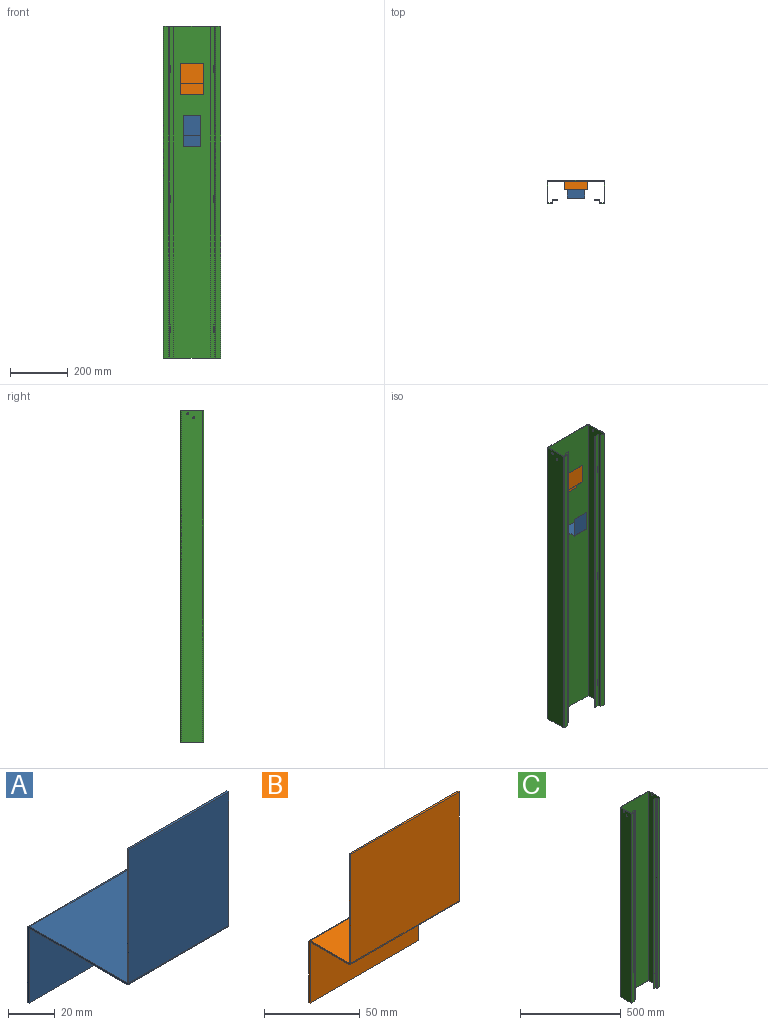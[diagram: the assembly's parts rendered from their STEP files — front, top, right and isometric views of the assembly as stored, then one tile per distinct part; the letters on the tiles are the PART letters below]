
ASSEMBLY  parts=3 mates=2
PART A: 22 faces, bbox 60x61x110 mm
  f0: plane 38.65x1mm, normal (-1,0,0), area 38.7mm2, adj f2,f3,f4,f19
  f1: plane 38.65x1mm, normal (1,0,0), area 38.7mm2, adj f2,f3,f4,f18
  f2: plane 60x1mm, normal (0,0,-1), area 60mm2, adj f0,f1,f3,f4
  f3: plane 60x38.65mm, normal (0,1,0), area 2319mm2, adj f0,f1,f2,f20
  f4: plane 60x38.65mm, normal (0,-1,0), area 2319mm2, adj f0,f1,f2,f21
  f5: plane 58.3x1mm, normal (-1,0,0), area 58.3mm2, adj f7,f8,f15,f19
  f6: plane 58.3x1mm, normal (1,0,0), area 58.3mm2, adj f7,f8,f14,f18
  f7: plane 60x58.3mm, normal (0,0,1), area 3498mm2, adj f5,f6,f17,f20
  f8: plane 60x58.3mm, normal (0,0,-1), area 3498mm2, adj f5,f6,f16,f21
  f9: plane 69.65x1mm, normal (-1,0,0), area 69.7mm2, adj f10,f12,f13,f15
  f10: plane 60x1mm, normal (0,0,1), area 60mm2, adj f9,f11,f12,f13
  f11: plane 69.65x1mm, normal (1,0,0), area 69.7mm2, adj f10,f12,f13,f14
  f12: plane 69.65x60mm, normal (0,1,0), area 4179mm2, adj f9,f10,f11,f17
  f13: plane 69.65x60mm, normal (0,-1,0), area 4179mm2, adj f9,f10,f11,f16
  f14: plane 1.35x1.35mm, normal (1,0,0), area 1.3mm2, adj f6,f11,f16,f17
  f15: plane 1.35x1.35mm, normal (-1,0,0), area 1.3mm2, adj f5,f9,f16,f17
  f16: cylinder r=1.35mm len=60mm, axis (1,0,0), area 127.2mm2, adj f8,f13,f14,f15
  f17: cylinder r=0.35mm len=60mm, axis (1,0,0), area 33mm2, adj f7,f12,f14,f15
  f18: plane 1.35x1.35mm, normal (1,0,0), area 1.3mm2, adj f1,f6,f20,f21
  f19: plane 1.35x1.35mm, normal (-1,0,0), area 1.3mm2, adj f0,f5,f20,f21
  f20: cylinder r=1.35mm len=60mm, axis (1,0,0), area 127.2mm2, adj f3,f7,f18,f19
  f21: cylinder r=0.35mm len=60mm, axis (1,0,0), area 33mm2, adj f4,f8,f18,f19
PART B: 22 faces, bbox 80x31x110 mm
  f0: plane 38.65x1mm, normal (-1,0,0), area 38.7mm2, adj f2,f3,f4,f19
  f1: plane 38.65x1mm, normal (1,0,0), area 38.7mm2, adj f2,f3,f4,f18
  f2: plane 80x1mm, normal (0,0,-1), area 80mm2, adj f0,f1,f3,f4
  f3: plane 80x38.65mm, normal (0,1,0), area 3092mm2, adj f0,f1,f2,f20
  f4: plane 80x38.65mm, normal (0,-1,0), area 3092mm2, adj f0,f1,f2,f21
  f5: plane 28.3x1mm, normal (-1,0,0), area 28.3mm2, adj f7,f8,f15,f19
  f6: plane 28.3x1mm, normal (1,0,0), area 28.3mm2, adj f7,f8,f14,f18
  f7: plane 80x28.3mm, normal (0,0,1), area 2264mm2, adj f5,f6,f17,f20
  f8: plane 80x28.3mm, normal (0,0,-1), area 2264mm2, adj f5,f6,f16,f21
  f9: plane 69.65x1mm, normal (-1,0,0), area 69.6mm2, adj f10,f12,f13,f15
  f10: plane 80x1mm, normal (0,0,1), area 80mm2, adj f9,f11,f12,f13
  f11: plane 69.65x1mm, normal (1,0,0), area 69.6mm2, adj f10,f12,f13,f14
  f12: plane 80x69.65mm, normal (0,1,0), area 5572mm2, adj f9,f10,f11,f17
  f13: plane 80x69.65mm, normal (0,-1,0), area 5572mm2, adj f9,f10,f11,f16
  f14: plane 1.35x1.35mm, normal (1,0,0), area 1.3mm2, adj f6,f11,f16,f17
  f15: plane 1.35x1.35mm, normal (-1,0,0), area 1.3mm2, adj f5,f9,f16,f17
  f16: cylinder r=1.35mm len=80mm, axis (1,0,0), area 169.6mm2, adj f8,f13,f14,f15
  f17: cylinder r=0.35mm len=80mm, axis (1,0,0), area 44mm2, adj f7,f12,f14,f15
  f18: plane 1.35x1.35mm, normal (1,0,0), area 1.3mm2, adj f1,f6,f20,f21
  f19: plane 1.35x1.35mm, normal (-1,0,0), area 1.3mm2, adj f0,f5,f20,f21
  f20: cylinder r=1.35mm len=80mm, axis (1,0,0), area 169.6mm2, adj f3,f7,f18,f19
  f21: cylinder r=0.35mm len=80mm, axis (1,0,0), area 44mm2, adj f4,f8,f18,f19
PART C: 98 faces, bbox 200x80x1150 mm
  f0: plane 1150x14.65mm, normal (0,1,0), area 16547.5mm2, adj f20,f21,f22,f25,f86,f87,f88,f89
  f1: plane 1150x14.65mm, normal (0,-1,0), area 16547.5mm2, adj f20,f21,f22,f26,f86,f87,f88,f89
  f2: plane 195.3x2mm, normal (0,0,1), area 390.6mm2, adj f4,f5,f36,f71
  f3: plane 195.3x2mm, normal (0,0,-1), area 390.6mm2, adj f4,f5,f35,f70
  f4: plane 1150x195.3mm, normal (0,-1,0), area 224595mm2, adj f2,f3,f38,f73
  f5: plane 1150x195.3mm, normal (0,1,0), area 224595mm2, adj f2,f3,f37,f72
  f6: plane 75.3x2mm, normal (0,0,1), area 150.6mm2, adj f10,f11,f32,f36
  f7: plane 75.3x2mm, normal (0,0,-1), area 150.6mm2, adj f10,f11,f31,f35
  f8: cylinder r=3.38mm len=6.76mm, axis (-1,0,0), area 42.5mm2, adj f10,f11
  f9: cylinder r=3.38mm len=6.76mm, axis (-1,0,0), area 42.5mm2, adj f10,f11
  f10: plane 1150x75.3mm, normal (-1,0,0), area 86523.3mm2, adj f6,f7,f8,f9,f34,f38
  f11: plane 1150x75.3mm, normal (1,0,0), area 86523.3mm2, adj f6,f7,f8,f9,f33,f37
  f12: plane 15.3x2mm, normal (0,0,1), area 30.6mm2, adj f14,f15,f28,f32
  f13: plane 15.3x2mm, normal (0,0,-1), area 30.6mm2, adj f14,f15,f27,f31
  f14: plane 1150x15.3mm, normal (0,1,0), area 17595mm2, adj f12,f13,f30,f34
  f15: plane 1150x15.3mm, normal (0,-1,0), area 17595mm2, adj f12,f13,f29,f33
  f16: plane 7.3x2mm, normal (0,0,1), area 14.6mm2, adj f18,f19,f24,f28
  f17: plane 7.3x2mm, normal (0,0,-1), area 14.6mm2, adj f18,f19,f23,f27
  f18: plane 1150x7.3mm, normal (1,0,0), area 8395mm2, adj f16,f17,f25,f30
  f19: plane 1150x7.3mm, normal (-1,0,0), area 8395mm2, adj f16,f17,f26,f29
  f20: plane 14.65x2mm, normal (0,0,1), area 29.3mm2, adj f0,f1,f22,f24
  f21: plane 14.65x2mm, normal (0,0,-1), area 29.3mm2, adj f0,f1,f22,f23
  f22: plane 1150x2mm, normal (-1,0,0), area 2300mm2, adj f0,f1,f20,f21
  f23: plane 2.35x2.35mm, normal (0,0,-1), area 4.2mm2, adj f17,f21,f25,f26
  f24: plane 2.35x2.35mm, normal (0,0,1), area 4.2mm2, adj f16,f20,f25,f26
  f25: cylinder r=2.35mm len=1150mm, axis (0,0,-1), area 4245.1mm2, adj f0,f18,f23,f24
  f26: cylinder r=0.35mm len=1150mm, axis (0,0,-1), area 632.2mm2, adj f1,f19,f23,f24
  f27: plane 2.35x2.35mm, normal (0,0,-1), area 4.2mm2, adj f13,f17,f29,f30
  f28: plane 2.35x2.35mm, normal (0,0,1), area 4.2mm2, adj f12,f16,f29,f30
  f29: cylinder r=2.35mm len=1150mm, axis (0,0,-1), area 4245.1mm2, adj f15,f19,f27,f28
  f30: cylinder r=0.35mm len=1150mm, axis (0,0,-1), area 632.2mm2, adj f14,f18,f27,f28
  f31: plane 2.35x2.35mm, normal (0,0,-1), area 4.2mm2, adj f7,f13,f33,f34
  f32: plane 2.35x2.35mm, normal (0,0,1), area 4.2mm2, adj f6,f12,f33,f34
  f33: cylinder r=2.35mm len=1150mm, axis (0,0,-1), area 4245.1mm2, adj f11,f15,f31,f32
  f34: cylinder r=0.35mm len=1150mm, axis (0,0,-1), area 632.2mm2, adj f10,f14,f31,f32
  f35: plane 2.35x2.35mm, normal (0,0,-1), area 4.2mm2, adj f3,f7,f37,f38
  f36: plane 2.35x2.35mm, normal (0,0,1), area 4.2mm2, adj f2,f6,f37,f38
  f37: cylinder r=2.35mm len=1150mm, axis (0,0,-1), area 4245.1mm2, adj f5,f11,f35,f36
  f38: cylinder r=0.35mm len=1150mm, axis (0,0,-1), area 632.2mm2, adj f4,f10,f35,f36
  f39: plane 75.3x2mm, normal (0,0,1), area 150.6mm2, adj f43,f44,f67,f71
  f40: plane 75.3x2mm, normal (0,0,-1), area 150.6mm2, adj f43,f44,f66,f70
  f41: cylinder r=3.38mm len=6.76mm, axis (1,0,0), area 42.5mm2, adj f43,f44
  f42: cylinder r=3.38mm len=6.76mm, axis (1,0,0), area 42.5mm2, adj f43,f44
  f43: plane 1150x75.3mm, normal (1,0,0), area 86523.3mm2, adj f39,f40,f41,f42,f69,f73
  f44: plane 1150x75.3mm, normal (-1,0,0), area 86523.3mm2, adj f39,f40,f41,f42,f68,f72
  f45: plane 15.3x2mm, normal (0,0,1), area 30.6mm2, adj f47,f48,f63,f67
  f46: plane 15.3x2mm, normal (0,0,-1), area 30.6mm2, adj f47,f48,f62,f66
  f47: plane 1150x15.3mm, normal (0,1,0), area 17595mm2, adj f45,f46,f65,f69
  f48: plane 1150x15.3mm, normal (0,-1,0), area 17595mm2, adj f45,f46,f64,f68
  f49: plane 7.3x2mm, normal (0,0,1), area 14.6mm2, adj f51,f52,f59,f63
  f50: plane 7.3x2mm, normal (0,0,-1), area 14.6mm2, adj f51,f52,f58,f62
  f51: plane 1150x7.3mm, normal (-1,0,0), area 8395mm2, adj f49,f50,f60,f65
  f52: plane 1150x7.3mm, normal (1,0,0), area 8395mm2, adj f49,f50,f61,f64
  f53: plane 14.65x2mm, normal (0,0,1), area 29.3mm2, adj f54,f56,f57,f59
  f54: plane 1150x2mm, normal (1,0,0), area 2300mm2, adj f53,f55,f56,f57
  f55: plane 14.65x2mm, normal (0,0,-1), area 29.3mm2, adj f54,f56,f57,f58
  f56: plane 1150x14.65mm, normal (0,1,0), area 16547.5mm2, adj f53,f54,f55,f60,f74,f76,f77,f78
  f57: plane 1150x14.65mm, normal (0,-1,0), area 16547.5mm2, adj f53,f54,f55,f61,f74,f76,f77,f78
  f58: plane 2.35x2.35mm, normal (0,0,-1), area 4.2mm2, adj f50,f55,f60,f61
  f59: plane 2.35x2.35mm, normal (0,0,1), area 4.2mm2, adj f49,f53,f60,f61
  f60: cylinder r=2.35mm len=1150mm, axis (0,0,-1), area 4245.1mm2, adj f51,f56,f58,f59,f75,f79,f83
  f61: cylinder r=0.35mm len=1150mm, axis (0,0,-1), area 632.2mm2, adj f52,f57,f58,f59,f75,f79,f83
  f62: plane 2.35x2.35mm, normal (0,0,-1), area 4.2mm2, adj f46,f50,f64,f65
  f63: plane 2.35x2.35mm, normal (0,0,1), area 4.2mm2, adj f45,f49,f64,f65
  f64: cylinder r=2.35mm len=1150mm, axis (0,0,-1), area 4245.1mm2, adj f48,f52,f62,f63
  f65: cylinder r=0.35mm len=1150mm, axis (0,0,-1), area 632.2mm2, adj f47,f51,f62,f63
  f66: plane 2.35x2.35mm, normal (0,0,-1), area 4.2mm2, adj f40,f46,f68,f69
  f67: plane 2.35x2.35mm, normal (0,0,1), area 4.2mm2, adj f39,f45,f68,f69
  f68: cylinder r=2.35mm len=1150mm, axis (0,0,-1), area 4245.1mm2, adj f44,f48,f66,f67
  f69: cylinder r=0.35mm len=1150mm, axis (0,0,-1), area 632.2mm2, adj f43,f47,f66,f67
  f70: plane 2.35x2.35mm, normal (0,0,-1), area 4.2mm2, adj f3,f40,f72,f73
  f71: plane 2.35x2.35mm, normal (0,0,1), area 4.2mm2, adj f2,f39,f72,f73
  f72: cylinder r=2.35mm len=1150mm, axis (0,0,-1), area 4245.1mm2, adj f5,f44,f70,f71
  f73: cylinder r=0.35mm len=1150mm, axis (0,0,-1), area 632.2mm2, adj f4,f43,f70,f71
  f74: plane 4x2mm, normal (0,0,-1), area 8mm2, adj f56,f57,f75,f77
  f75: plane 25x2mm, normal (1,0,0), area 50mm2, adj f60,f61,f74,f76
  f76: plane 4x2mm, normal (0,0,1), area 8mm2, adj f56,f57,f75,f77
  f77: plane 25x2mm, normal (-1,0,0), area 50mm2, adj f56,f57,f74,f76
  f78: plane 4x2mm, normal (0,0,-1), area 8mm2, adj f56,f57,f79,f81
  f79: plane 25x2mm, normal (1,0,0), area 50mm2, adj f60,f61,f78,f80
  f80: plane 4x2mm, normal (0,0,1), area 8mm2, adj f56,f57,f79,f81
  f81: plane 25x2mm, normal (-1,0,0), area 50mm2, adj f56,f57,f78,f80
  f82: plane 4x2mm, normal (0,0,-1), area 8mm2, adj f56,f57,f83,f85
  f83: plane 25x2mm, normal (1,0,0), area 50mm2, adj f60,f61,f82,f84
  f84: plane 4x2mm, normal (0,0,1), area 8mm2, adj f56,f57,f83,f85
  f85: plane 25x2mm, normal (-1,0,0), area 50mm2, adj f56,f57,f82,f84
  f86: plane 4x2mm, normal (0,0,-1), area 8mm2, adj f0,f1,f87,f89
  f87: plane 25x2mm, normal (1,0,0), area 50mm2, adj f0,f1,f86,f88
  f88: plane 4x2mm, normal (0,0,1), area 8mm2, adj f0,f1,f87,f89
  f89: plane 25x2mm, normal (-1,0,0), area 50mm2, adj f0,f1,f86,f88
  f90: plane 4x2mm, normal (0,0,-1), area 8mm2, adj f0,f1,f91,f93
  f91: plane 25x2mm, normal (1,0,0), area 50mm2, adj f0,f1,f90,f92
  f92: plane 4x2mm, normal (0,0,1), area 8mm2, adj f0,f1,f91,f93
  f93: plane 25x2mm, normal (-1,0,0), area 50mm2, adj f0,f1,f90,f92
  f94: plane 4x2mm, normal (0,0,-1), area 8mm2, adj f0,f1,f95,f97
  f95: plane 25x2mm, normal (1,0,0), area 50mm2, adj f0,f1,f94,f96
  f96: plane 4x2mm, normal (0,0,1), area 8mm2, adj f0,f1,f95,f97
  f97: plane 25x2mm, normal (-1,0,0), area 50mm2, adj f0,f1,f94,f96
PLACE A t=(-324.63,-390.04,-487.98)mm
PLACE B t=(-324.63,-405.5,-455.3)mm
PLACE C t=(-324.63,-428.04,-109.33)mm fixed
MATE fastened A.f3 <-> C.f4  axis (0,1,0) through (-324.63,-390.04,-489.33)mm
MATE fastened C.f4 <-> B.f3  axis (0,-1,0) through (-324.63,-390.04,-309.33)mm
